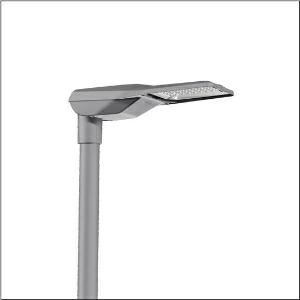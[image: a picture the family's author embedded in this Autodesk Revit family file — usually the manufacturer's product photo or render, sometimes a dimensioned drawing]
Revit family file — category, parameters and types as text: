
# Revit family: streetlight_sl_21_iq_mini___st0_5a_5xe2b41g08hb_4387
name_source: partatom
category: Lighting Fixtures
units: mm (PartAtom-declared; Revit-internal decimal feet)

## family parameters
Cut with Voids When Loaded = No
Host = Face
Light Source = No
Part Type = Normal
Room Calculation Point = No
Round Connector Dimension = Use Diameter
Shared = No

## types (1)
- --- (1 x LED, 9860 lm, 70.9 W, 4000K)
    Apparent Load = 71 VA
    CIE Flux Codes = 41 75 97 100 100
    Color Rendering = 70
    Color Temperature = 4000K
    Default Elevation = 1800 mm
    Description = Streetlight SL 21 iQ mini, mast luminaire, primary light control with lens, of PMMA, primary optical cover: cover, of toughened safety glass, transparent, light distribution: ST0.5a, light emission: direct distribution, primary light characteristic: asymmetric, installation type: post-top, side-entry, LED, High Power LED, rated luminous flux: 9.860lm, luminous efficacy: 139lm/W, light colour: 740, colour temperature: 4000K, control: Street-Remote, Auto-Match, Temp-Guard, Lumen-Switch, Night-Set, Smart-Wire, Light-Fading, Desk-Remote (wireless, voltage-free reading and setting of iQ features in the workshop via application-optimized NFC function/RFID function), optimised constant luminous flux control (CLO 2.0), presetting dimming linear, mains connection: 220..240V, AC, 50/60Hz, start of lifetime: 71W, end of service life: 75W, reduction: 31W, luminaire housing, of diecast aluminium, powder-coated, Siteco® metallic grey (DB 702S), corrosivity category C5 mid according to DIN EN ISO 12944, please order mast flange separately, inclination adjustable: 0°, 5°, 10°, 15°, sealing non-destructively replaceable, multi-level sealing system, length: 628mm, width: 235mm, height: 110mm, mast flange for spigot size: 42mm (side-entry): 5XC10008XM4, 60/48mm (side-entry/post-top): 5XC10108XM2, 76/60mm (side-entry/post-top): 5XC10108XM1, protection rating (complete): IP66, insulation class (complete): insulation class II (safety insulation), certification: CE, ENEC, ENEC+, VDE, impact resistance: IK09, permissible operating ambient temperature for outdoor applications: -40..+50°C, standard-compliant lighting for roads and squares, packaging unit: 1 piece

Light Distribution: ST0.5a
    Height = 110 mm
    Lamp = 1 x LED
    Lamp Light Flux = 9860 lm
    Lamp Power = 70.9 W
    Lamp count = 1
    Length = 625 mm
    Luminous efficacy = 139 lm/W
    Manufacturer = Siteco
    ModVariant = No
    Model = 5XE2B41G08HB
    Number of Poles = 1
    OnlyDefault = Yes
    Power Factor = 1
    Product Name = Streetlight SL 21 iQ mini | ST0.5a
    Product group = mast luminaire | pylon top
    ProductGroupID = 6100
    Protection Class = Protection class II
    Protection Degree = IP 66
    RLX_Detail_Level = 1
    RLX_Emergency_Light_Flux = 0 lm
    RLX_Emergency_Type = 0
    RLX_Emergency_Type_DB = No
    RlxData = <blob elided: 103321 chars, md5=3538c07b>
    Socket = socket
    Standby Power = 0 W
    System Light Flux = 9860 lm
    System Power = 71 W
    Type Comments = factory setting: luminous flux: 100 % | dim-lin: 254 | 711 mA
    Type Image = l_1003519.jpg
    URL = http://relux.com
    VarID = @adj_090837
    Voltage = 0 V
    Weight = 0.00 kg
    Width = 234 mm

## geometry (parser evidence)
native form markers: Blend x4, Sweep x9
no freeform markers — native parametric forms only
